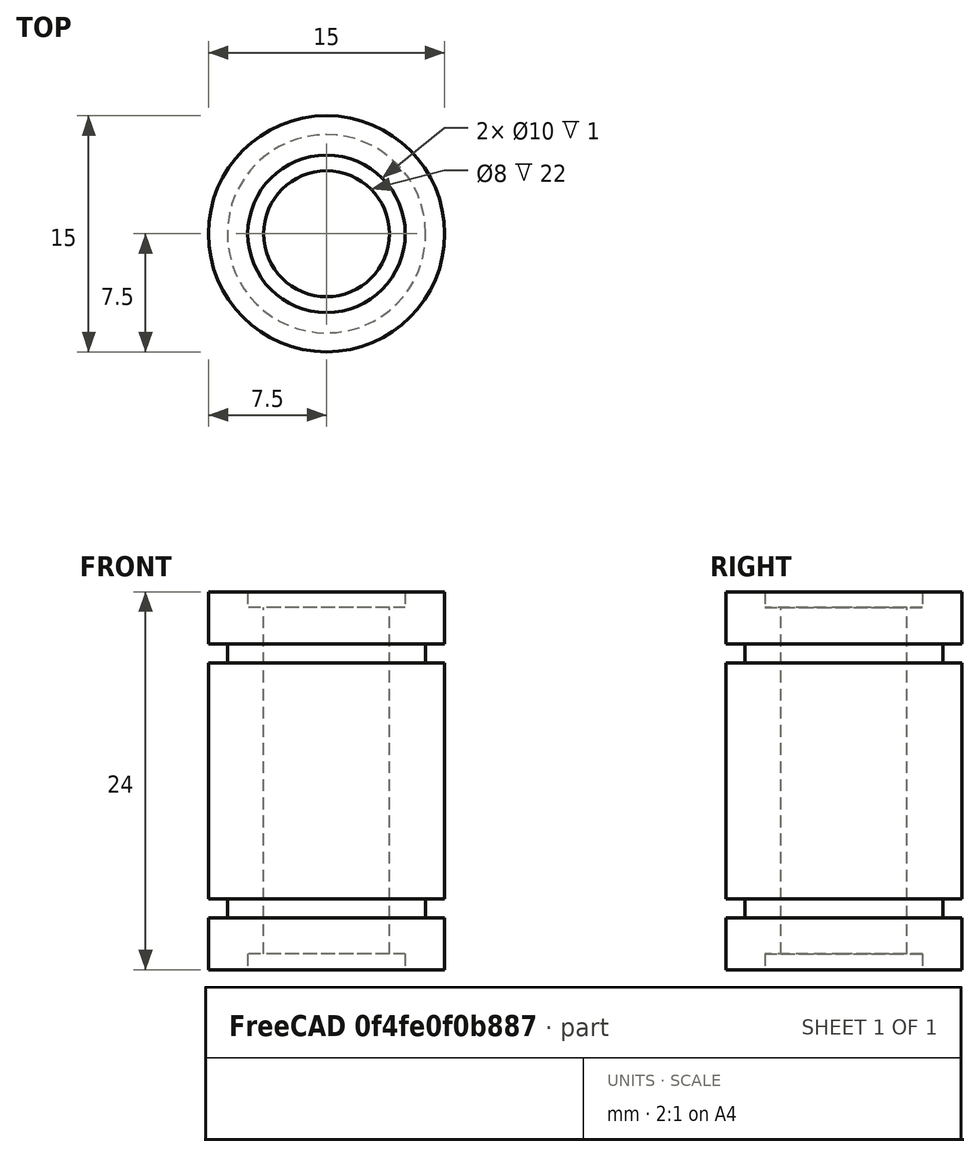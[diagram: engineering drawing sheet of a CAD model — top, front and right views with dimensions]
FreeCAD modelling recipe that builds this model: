
FCSTD DOCUMENT  (FreeCAD 1.0R39109 (Git))
Label: 1_2_linear_bearing_simple
License: All rights reserved
LicenseURL: https://en.wikipedia.org/wiki/All_rights_reserved
objects: Sketcher::SketchObject×1, PartDesign::Revolution×1, PartDesign::Body×1
note: 6 computed .brp shape members not serialized (recipe doc carries the construction recipe); baked Part::Feature solids carry a one-line shape summary decoded from their .brp

FEATURE [Sketcher::SketchObject] Sketch
  ArcFitTolerance = 1e-06
  AttachmentSupport = -> [XZ_Plane]
  FullyConstrained = true
  MakeInternals = false
  MapMode = 5
  Placement = pos=(0,0,0) rot=(1,0,0;1.5708rad)
  sketch-geometry (16):
    g0: LineSegment StartX=4 StartY=1 StartZ=0 EndX=4 EndY=23 EndZ=0
    g1: LineSegment StartX=7.5 StartY=24 StartZ=0 EndX=7.5 EndY=20.7 EndZ=0
    g2: LineSegment StartX=7.5 StartY=20.7 StartZ=0 EndX=6.3 EndY=20.7 EndZ=0
    g3: LineSegment StartX=6.3 StartY=20.7 StartZ=0 EndX=6.3 EndY=19.5 EndZ=0
    g4: LineSegment StartX=6.3 StartY=19.5 StartZ=0 EndX=7.5 EndY=19.5 EndZ=0
    g5: LineSegment StartX=7.5 StartY=19.5 StartZ=0 EndX=7.5 EndY=4.5 EndZ=0
    g6: LineSegment StartX=7.5 StartY=4.5 StartZ=0 EndX=6.3 EndY=4.5 EndZ=0
    g7: LineSegment StartX=6.3 StartY=4.5 StartZ=0 EndX=6.3 EndY=3.3 EndZ=0
    g8: LineSegment StartX=6.3 StartY=3.3 StartZ=0 EndX=7.5 EndY=3.3 EndZ=0
    g9: LineSegment StartX=7.5 StartY=3.3 StartZ=0 EndX=7.5 EndY=0 EndZ=0
    g10: LineSegment StartX=4 StartY=1 StartZ=0 EndX=5 EndY=1 EndZ=0
    g11: LineSegment StartX=5 StartY=1 StartZ=0 EndX=5 EndY=0 EndZ=0
    g12: LineSegment StartX=5 StartY=0 StartZ=0 EndX=7.5 EndY=0 EndZ=0
    g13: LineSegment StartX=7.5 StartY=24 StartZ=0 EndX=5 EndY=24 EndZ=0
    g14: LineSegment StartX=5 StartY=24 StartZ=0 EndX=5 EndY=23 EndZ=0
    g15: LineSegment StartX=5 StartY=23 StartZ=0 EndX=4 EndY=23 EndZ=0
  constraints (48):
    c: Vertical(g0)
    c: Vertical(g1)
    c: Coincident(g1,g2)
    c: Coincident(g2,g3)
    c: Coincident(g3,g4)
    c: Coincident(g4,g5)
    c: Vertical(g5)
    c: Coincident(g5,g6)
    c: Coincident(g6,g7)
    c: Coincident(g7,g8)
    c: Coincident(g8,g9)
    c: Vertical(g9)
    c: Horizontal(g2)
    c: Vertical(g3)
    c: Horizontal(g4)
    c: Horizontal(g6)
    c: Vertical(g7)
    c: Horizontal(g8)
    c: Vertical(g5,g8)
    c: Vertical(g4,g1)
    c: DistanceY(g5,g5) = 15
    c: Vertical(g3,g6)
    c: Equal(g1,g9)
    c: Equal(g3,g7)
    c: PointOnObject(g9,g-1)
    c: Coincident(g0,g10)
    c: Horizontal(g10)
    c: Coincident(g10,g11)
    c: Vertical(g11)
    c: Coincident(g11,g12)
    c: Coincident(g12,g9)
    c: Horizontal(g12)
    c: Coincident(g1,g13)
    c: Horizontal(g13)
    c: Coincident(g13,g14)
    c: Coincident(g14,g15)
    c: Coincident(g15,g0)
    c: Horizontal(g15)
    c: Vertical(g14)
    c: Vertical(g14,g10)
    c: Distance(g12,g13) = 24
    c: Equal(g14,g11)
    c: DistanceY(g0,g0) = 22
    c: Distance(g-2,g0) = 4
    c: DistanceX(g15,g15) = 1
    c: Distance(g-2,g5) = 7.5
    c: DistanceY(g3,g3) = 1.2
    c: DistanceX(g2,g2) = 1.2
FEATURE [PartDesign::Revolution] Revolution
  Angle = 360
  Angle2 = 60
  Axis = (0,2e-16,1)
  Base = (0,0,0)
  Placement = pos=(0,0,0) rot=(1,0,0;1.5708rad)
  Profile = -> Sketch
  ReferenceAxis = -> Sketch [V_Axis]
  Refine = true
  Reversed = true
  Suppressed = false
  Type = 0
FEATURE [PartDesign::Body] Body
  AllowCompound = false
  Group = -> [Sketch,Revolution]
  Origin = -> Origin
  Tip = -> Revolution
